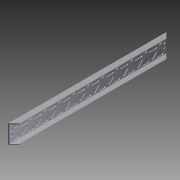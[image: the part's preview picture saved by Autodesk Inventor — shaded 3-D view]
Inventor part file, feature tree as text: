
AUTODESK INVENTOR PART (.ipt)
format: ipt  version: 2012 (Build 160160000, 160)  size: 526,848 bytes
history: native  units: in
note: dims shown in document units (in); Inventor stores cm internally (conversion verified against a paired STEP export)
features: extrude x3, sketch x3, fillet x1
ambient origin geometry x8: Origin, YZ Plane, XZ Plane, XY Plane, X Axis, Y Axis, Z Axis, Center Point
bodies: Solid1 (feature_tree)
feature tree (7):
  extrude  "Extrusion1"  Depth=1.0in
  extrude  "Extrusion2"  Depth=0.125in
  extrude  "Extrusion3"  Depth=0.125in
  fillet  "Fillet1"  Radius=28.0in
  sketch  "Sketch1"  dims[d0=3.25in d1=1.0in]
  sketch  "Sketch2"  dims[d2=1.0in d3=0.125in]
  sketch  "Sketch3"  dims[d4=0.125in d5=0.125in d6=28.0in d7=0.0in d8=45.0deg d9=1.0in d10=0.0in d11=0.5232in d12=0.2616in d13=0.25in d14=0.125in d15=0.125in d16=0.125in d17=0.125in d18=0.25in d19=0.125in d20=0.125in d21=0.25in d22=0.125in d23=0.125in d24=0.25in d25=0.125in d26=0.125in d27=0.125in d28=0.125in d29=0.125in d30=0.125in d31=0.125in d32=0.25in d34=2.5455in d35=3.937in d37=2.5455in d38=0.3937in d40=1.0in d42=0.125in d43=0.125in d44=0.125in d45=0.125in d46=0.25in d47=0.125in d48=0.125in d49=0.25in d50=0.125in d51=0.25in d52=0.125in d53=0.25in d54=1.0in d55=0.0in d56=0.25in]
